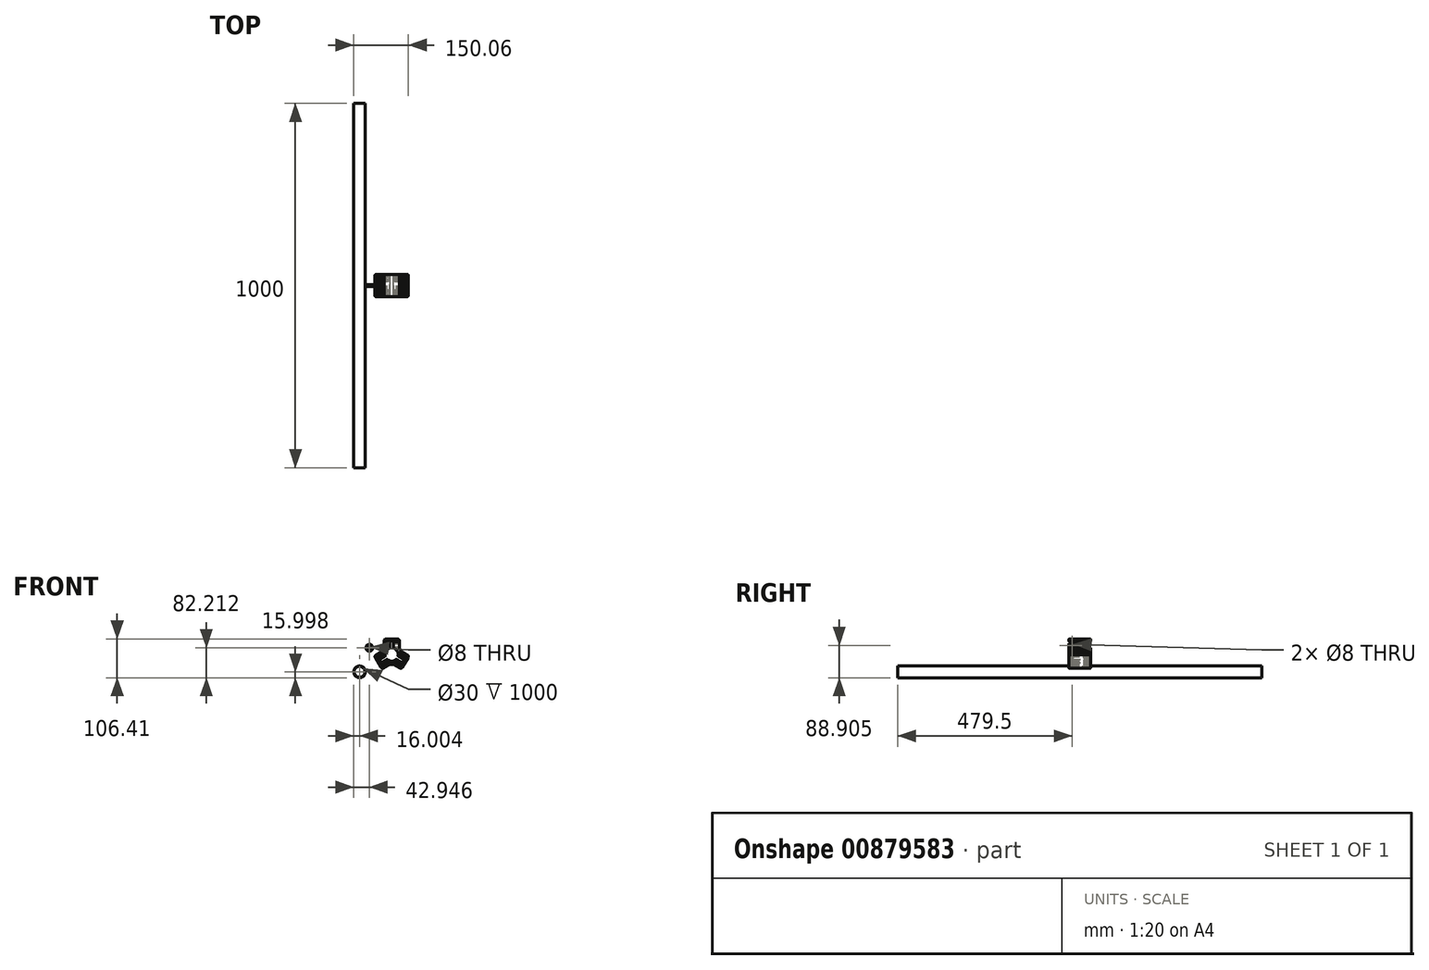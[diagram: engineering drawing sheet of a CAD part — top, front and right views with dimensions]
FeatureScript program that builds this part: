
annotation { "Feature Type Name" : "Feature", "Feature Type Description" : "" }
export const myFeature = defineFeature(function(context is Context, id is Id, definition is map)
    precondition{}
    {
        {
            var Q0;
            Q0=qCreatedBy(makeId("Front.planeOp"),FACE);
            var sketch = newSketch(context, id + "F0", { "sketchPlane" : qUnion([Q0])});
            skCircle(sketch, "E0", {"center": v(-38.83, 28.74) * mm, "radius": 9.5 * mm});
            skCircle(sketch, "E1", {"center": v(-38.83, 28.74) * mm, "radius": 4 * mm});
            skSolve(sketch);
        }
        {
            var Q0;
            Q0 = qSketchRegion(id + "F0", true);
            extrude(context, id + "F1", {"entities" : qUnion([Q0]), "endBound" : BoundingType.SYMMETRIC, "depth" : 6 * mm, "offsetDistance" : 25 * mm});
        }
        {
            var Q0;
            Q0=makeQuery(id+"F1.opExtrude","CAP_EDGE",EDGE,{"disambiguationData":[OSD([sQuery(id+"F0.wireOp",EDGE,"E0")])],"isStart":false});
            var Q1;
            Q1=makeQuery(id+"F1.opExtrude","CAP_EDGE",EDGE,{"disambiguationData":[OSD([sQuery(id+"F0.wireOp",EDGE,"E1")])],"isStart":false});
            var Q2;
            Q2=makeQuery(id+"F1.opExtrude","CAP_EDGE",EDGE,{"disambiguationData":[OSD([sQuery(id+"F0.wireOp",EDGE,"E0")])],"isStart":true});
            var Q3;
            Q3=makeQuery(id+"F1.opExtrude","CAP_EDGE",EDGE,{"disambiguationData":[OSD([sQuery(id+"F0.wireOp",EDGE,"E1")])],"isStart":true});
            fillet(context, id + "F2", {"entities" : qUnion([Q0, Q1, Q2, Q3]), "radius" : 0.2 * mm, "tangentPropagation" : true, "allowEdgeOverflow" : false});
        }
        {
            var Q0;
            Q0=qCreatedBy(makeId("Front.planeOp"),FACE);
            var sketch = newSketch(context, id + "F3", { "sketchPlane" : qUnion([Q0])});
            skCircle(sketch, "E2", {"center": v(22.48, 9.94) * mm, "radius": 16 * mm});
            skLineSegment(sketch, "E3.bottom", {"start": v(19.48, 25.94) * mm, "end": v(25.48, 25.94) * mm});
            skLineSegment(sketch, "E3.top", {"start": v(19.48, 44.94) * mm, "end": v(25.48, 44.94) * mm});
            skLineSegment(sketch, "E3.left", {"start": v(19.48, 25.94) * mm, "end": v(19.48, 44.94) * mm});
            skLineSegment(sketch, "E3.right", {"start": v(25.48, 25.94) * mm, "end": v(25.48, 44.94) * mm});
            skPoint(sketch, "E4", {"position": v(22.48, 25.94) * mm});
            skLineSegment(sketch, "E5.1.0", {"start": v(-6.33, -10.16) * mm, "end": v(-9.33, -4.97) * mm});
            skLineSegment(sketch, "E5.1.1", {"start": v(10.12, -0.66) * mm, "end": v(-6.33, -10.16) * mm});
            skLineSegment(sketch, "E5.1.2", {"start": v(7.12, 4.53) * mm, "end": v(-9.33, -4.97) * mm});
            skLineSegment(sketch, "E5.1.3", {"start": v(10.12, -0.66) * mm, "end": v(7.12, 4.53) * mm});
            skLineSegment(sketch, "E5.2.0", {"start": v(54.29, -4.97) * mm, "end": v(51.29, -10.16) * mm});
            skLineSegment(sketch, "E5.2.1", {"start": v(37.83, 4.53) * mm, "end": v(54.29, -4.97) * mm});
            skLineSegment(sketch, "E5.2.2", {"start": v(34.83, -0.66) * mm, "end": v(51.29, -10.16) * mm});
            skLineSegment(sketch, "E5.2.3", {"start": v(37.83, 4.53) * mm, "end": v(34.83, -0.66) * mm});
            skArc(sketch, "E6", {"start": v(16.18, 26.8) * mm, "mid": v(6.89, 18.93) * mm, "end": v(4.73, 6.96) * mm});
            skArc(sketch, "E7.trimOffspring", {"start": v(40.23, 6.96) * mm, "mid": v(38.06, 18.93) * mm, "end": v(28.78, 26.8) * mm});
            skArc(sketch, "E8.trimOffspring", {"start": v(11.03, -3.95) * mm, "mid": v(22.48, -8.06) * mm, "end": v(33.93, -3.95) * mm});
            skLineSegment(sketch, "E9.0", {"start": v(27.48, 28.67) * mm, "end": v(27.48, 45.94) * mm});
            skLineSegment(sketch, "E9.1", {"start": v(18.48, 46.94) * mm, "end": v(26.48, 46.94) * mm});
            skLineSegment(sketch, "E9.2", {"start": v(17.48, 28.67) * mm, "end": v(17.48, 45.94) * mm});
            skLineSegment(sketch, "E10", {"start": v(27.48, 46.94) * mm, "end": v(27.48, 52.94) * mm, "construction": true});
            skLineSegment(sketch, "E11", {"start": v(1.7, 27.32) * mm, "end": v(1.7, 47.94) * mm});
            skLineSegment(sketch, "E12", {"start": v(6.7, 52.94) * mm, "end": v(38.26, 52.94) * mm});
            skLineSegment(sketch, "E13.1.0", {"start": v(17.81, -16.76) * mm, "end": v(-0.04, -27.06) * mm});
            skLineSegment(sketch, "E13.1.1", {"start": v(-6.87, -25.23) * mm, "end": v(-22.65, 2.1) * mm});
            skLineSegment(sketch, "E13.1.2", {"start": v(-2.97, 19.24) * mm, "end": v(-20.82, 8.93) * mm});
            skLineSegment(sketch, "E13.2.0", {"start": v(47.92, 19.24) * mm, "end": v(65.78, 8.93) * mm});
            skLineSegment(sketch, "E13.2.1", {"start": v(67.6, 2.1) * mm, "end": v(51.82, -25.23) * mm});
            skLineSegment(sketch, "E13.2.2", {"start": v(27.14, -16.76) * mm, "end": v(45, -27.06) * mm});
            skPoint(sketch, "E14.visualSharp", {"position": v(1.7, 52.94) * mm});
            skArc(sketch, "E14.filletArc", {"start": v(6.7, 52.94) * mm, "mid": v(3.16, 51.47) * mm, "end": v(1.7, 47.94) * mm});
            skPoint(sketch, "E15.visualSharp", {"position": v(-25.15, 6.43) * mm});
            skArc(sketch, "E15.filletArc", {"start": v(-20.82, 8.93) * mm, "mid": v(-23.15, 5.9) * mm, "end": v(-22.65, 2.1) * mm});
            skPoint(sketch, "E16.visualSharp", {"position": v(-4.37, -29.56) * mm});
            skArc(sketch, "E16.filletArc", {"start": v(-6.87, -25.23) * mm, "mid": v(-3.84, -27.56) * mm, "end": v(-0.04, -27.06) * mm});
            skPoint(sketch, "E17.visualSharp", {"position": v(49.32, -29.56) * mm});
            skArc(sketch, "E17.filletArc", {"start": v(45, -27.06) * mm, "mid": v(48.79, -27.56) * mm, "end": v(51.82, -25.23) * mm});
            skPoint(sketch, "E18.visualSharp", {"position": v(70.1, 6.43) * mm});
            skArc(sketch, "E18.filletArc", {"start": v(67.6, 2.1) * mm, "mid": v(68.1, 5.9) * mm, "end": v(65.78, 8.93) * mm});
            skLineSegment(sketch, "E19", {"start": v(43.26, 47.94) * mm, "end": v(43.26, 27.32) * mm});
            skPoint(sketch, "E20.visualSharp", {"position": v(43.26, 52.94) * mm});
            skArc(sketch, "E20.filletArc", {"start": v(43.26, 47.94) * mm, "mid": v(41.8, 51.47) * mm, "end": v(38.26, 52.94) * mm});
            skLineSegment(sketch, "E21.1.0", {"start": v(8.75, -3.76) * mm, "end": v(-6.2, -12.4) * mm});
            skLineSegment(sketch, "E21.1.1", {"start": v(-7.57, -12.03) * mm, "end": v(-11.57, -5.1) * mm});
            skLineSegment(sketch, "E21.1.2", {"start": v(3.75, 4.9) * mm, "end": v(-11.2, -3.73) * mm});
            skLineSegment(sketch, "E21.2.0", {"start": v(41.2, 4.9) * mm, "end": v(56.15, -3.73) * mm});
            skLineSegment(sketch, "E21.2.1", {"start": v(56.52, -5.1) * mm, "end": v(52.52, -12.03) * mm});
            skLineSegment(sketch, "E21.2.2", {"start": v(36.2, -3.76) * mm, "end": v(51.15, -12.4) * mm});
            skPoint(sketch, "E22.visualSharp", {"position": v(10, -3.04) * mm});
            skArc(sketch, "E22.filletArc", {"start": v(11.03, -3.95) * mm, "mid": v(9.92, -3.5) * mm, "end": v(8.75, -3.76) * mm});
            skPoint(sketch, "E23.visualSharp", {"position": v(34.95, -3.04) * mm});
            skArc(sketch, "E23.filletArc", {"start": v(36.2, -3.76) * mm, "mid": v(35.03, -3.5) * mm, "end": v(33.93, -3.95) * mm});
            skPoint(sketch, "E24.visualSharp", {"position": v(39.95, 5.62) * mm});
            skArc(sketch, "E24.filletArc", {"start": v(40.23, 6.96) * mm, "mid": v(40.4, 5.78) * mm, "end": v(41.2, 4.9) * mm});
            skPoint(sketch, "E25.visualSharp", {"position": v(27.48, 27.22) * mm});
            skArc(sketch, "E25.filletArc", {"start": v(27.48, 28.67) * mm, "mid": v(27.83, 27.53) * mm, "end": v(28.78, 26.8) * mm});
            skPoint(sketch, "E26.visualSharp", {"position": v(17.48, 27.22) * mm});
            skArc(sketch, "E26.filletArc", {"start": v(16.18, 26.8) * mm, "mid": v(17.12, 27.53) * mm, "end": v(17.48, 28.67) * mm});
            skPoint(sketch, "E27.visualSharp", {"position": v(5, 5.62) * mm});
            skArc(sketch, "E27.filletArc", {"start": v(3.75, 4.9) * mm, "mid": v(4.56, 5.78) * mm, "end": v(4.73, 6.96) * mm});
            skPoint(sketch, "E28.visualSharp", {"position": v(17.48, 46.94) * mm});
            skArc(sketch, "E28.filletArc", {"start": v(18.48, 46.94) * mm, "mid": v(17.77, 46.64) * mm, "end": v(17.48, 45.94) * mm});
            skPoint(sketch, "E29.visualSharp", {"position": v(27.48, 46.94) * mm});
            skArc(sketch, "E29.filletArc", {"start": v(27.48, 45.94) * mm, "mid": v(27.18, 46.64) * mm, "end": v(26.48, 46.94) * mm});
            skPoint(sketch, "E30.visualSharp", {"position": v(57.02, -4.23) * mm});
            skArc(sketch, "E30.filletArc", {"start": v(56.52, -5.1) * mm, "mid": v(56.62, -4.34) * mm, "end": v(56.15, -3.73) * mm});
            skPoint(sketch, "E31.visualSharp", {"position": v(52.02, -12.9) * mm});
            skArc(sketch, "E31.filletArc", {"start": v(51.15, -12.4) * mm, "mid": v(51.91, -12.5) * mm, "end": v(52.52, -12.03) * mm});
            skPoint(sketch, "E32.visualSharp", {"position": v(-7.07, -12.9) * mm});
            skArc(sketch, "E32.filletArc", {"start": v(-7.57, -12.03) * mm, "mid": v(-6.96, -12.5) * mm, "end": v(-6.2, -12.4) * mm});
            skPoint(sketch, "E33.visualSharp", {"position": v(-12.07, -4.23) * mm});
            skArc(sketch, "E33.filletArc", {"start": v(-11.2, -3.73) * mm, "mid": v(-11.67, -4.34) * mm, "end": v(-11.57, -5.1) * mm});
            skArc(sketch, "E34", {"start": v(1.7, 27.32) * mm, "mid": v(-1, 23.48) * mm, "end": v(-2.97, 19.24) * mm});
            skArc(sketch, "E35.trimOffspring", {"start": v(47.92, 19.24) * mm, "mid": v(45.94, 23.48) * mm, "end": v(43.26, 27.32) * mm});
            skArc(sketch, "E36.trimOffspring", {"start": v(17.81, -16.76) * mm, "mid": v(22.48, -17.16) * mm, "end": v(27.14, -16.76) * mm});
            skPoint(sketch, "E37.orphan", {"position": v(1.7, 21.93) * mm});
            skPoint(sketch, "E38.orphan", {"position": v(43.26, 21.93) * mm});
            skPoint(sketch, "E39.orphan", {"position": v(22.48, -14.06) * mm});
            skSolve(sketch);
        }
        {
            var Q0;
            Q0 = qSketchRegion(id + "F3", true);
            extrude(context, id + "F4", {"entities" : qUnion([Q0]), "endBound" : BoundingType.SYMMETRIC, "depth" : 60 * mm, "offsetDistance" : 25 * mm});
        }
        {
            var Q0;
            Q0=makeQuery(id+"F4.opExtrude","SWEPT_FACE",FACE,{"disambiguationData":[OSD([sQuery(id+"F3.wireOp",EDGE,"E9.0")])]});
            var sketch = newSketch(context, id + "F5", { "sketchPlane" : qUnion([Q0])});
            skCircle(sketch, "E40", {"center": v(20.5, 35.44) * mm, "radius": 9.5 * mm});
            skPoint(sketch, "E41", {"position": v(30, 35.44) * mm});
            skPoint(sketch, "E42", {"position": v(20.5, 44.94) * mm});
            skCircle(sketch, "E43", {"center": v(20.5, 35.44) * mm, "radius": 4 * mm});
            skLineSegment(sketch, "E44", {"start": v(0, 28.67) * mm, "end": v(0, 37.9) * mm});
            skCircle(sketch, "E45.MirrorC", {"center": v(-20.5, 35.44) * mm, "radius": 4 * mm});
            skLineSegment(sketch, "E46", {"start": v(20.5, 35.44) * mm, "end": v(20.5, 28.67) * mm});
            skSolve(sketch);
        }
        {
            var Q0;
            Q0=makeQuery(id+"F5.imprint","IMPRINT",FACE,{"disambiguationData":[TD([[makeQuery(id+"F5.imprint","IMPRINT",EDGE,{"derivedFrom":sQuery(id+"F5.wireOp",EDGE,"E43")}),1.0]])]});
            extrude(context, id + "F6", {"entities" : qUnion([Q0]), "operationType" : NewBodyOperationType.REMOVE, "endBound" : BoundingType.SYMMETRIC, "depth" : 55.2 * mm, "offsetDistance" : 25 * mm});
        }
        {
            var Q0;
            Q0=makeQuery(id+"F5.imprint","IMPRINT",FACE,{"disambiguationData":[TD([[makeQuery(id+"F5.imprint","IMPRINT",EDGE,{"derivedFrom":sQuery(id+"F5.wireOp",EDGE,"E45.MirrorC")}),-1.0]])]});
            extrude(context, id + "F7", {"entities" : qUnion([Q0]), "operationType" : NewBodyOperationType.REMOVE, "endBound" : BoundingType.SYMMETRIC, "depth" : 66 * mm, "offsetDistance" : 25 * mm});
        }
        {
            var Q0;
            Q0=makeQuery(id+"F4.opExtrude","SWEPT_FACE",FACE,{"disambiguationData":[OSD([sQuery(id+"F3.wireOp",EDGE,"E21.1.0")])]});
            var sketch = newSketch(context, id + "F8", { "sketchPlane" : qUnion([Q0])});
            skCircle(sketch, "E47", {"center": v(-1.07, 20.5) * mm, "radius": 9.5 * mm});
            skPoint(sketch, "E48", {"position": v(-1.07, 30) * mm});
            skPoint(sketch, "E49", {"position": v(-10.57, 20.5) * mm});
            skCircle(sketch, "E50", {"center": v(-1.07, 20.5) * mm, "radius": 4 * mm});
            skLineSegment(sketch, "E51", {"start": v(5.7, 0) * mm, "end": v(-4.1, 0) * mm});
            skCircle(sketch, "E52.MirrorC", {"center": v(-1.07, -20.5) * mm, "radius": 4 * mm});
            skLineSegment(sketch, "E53", {"start": v(-1.07, 20.5) * mm, "end": v(5.7, 20.5) * mm});
            skSolve(sketch);
        }
        {
            var Q0;
            Q0=makeQuery(id+"F8.imprint","IMPRINT",FACE,{"disambiguationData":[TD([[makeQuery(id+"F8.imprint","IMPRINT",EDGE,{"derivedFrom":sQuery(id+"F8.wireOp",EDGE,"E52.MirrorC")}),-1.0]])]});
            var Q1;
            Q1=makeQuery(id+"F8.imprint","IMPRINT",FACE,{"disambiguationData":[TD([[makeQuery(id+"F8.imprint","IMPRINT",EDGE,{"derivedFrom":sQuery(id+"F8.wireOp",EDGE,"E50")}),1.0]])]});
            extrude(context, id + "F9", {"entities" : qUnion([Q0, Q1]), "operationType" : NewBodyOperationType.REMOVE, "endBound" : BoundingType.SYMMETRIC, "depth" : 59.8 * mm, "offsetDistance" : 25 * mm});
        }
        {
            var Q0;
            Q0=makeQuery(id+"F4.opExtrude","SWEPT_FACE",FACE,{"disambiguationData":[OSD([sQuery(id+"F3.wireOp",EDGE,"E21.2.0")])]});
            var sketch = newSketch(context, id + "F10", { "sketchPlane" : qUnion([Q0])});
            skCircle(sketch, "E54", {"center": v(40, -20.5) * mm, "radius": 9.5 * mm});
            skPoint(sketch, "E55", {"position": v(49.5, -20.5) * mm});
            skPoint(sketch, "E56", {"position": v(40, -30) * mm});
            skCircle(sketch, "E57", {"center": v(40, -20.5) * mm, "radius": 4 * mm});
            skLineSegment(sketch, "E58", {"start": v(33.23, 0) * mm, "end": v(40.2, 0) * mm});
            skCircle(sketch, "E59.MirrorC", {"center": v(40, 20.5) * mm, "radius": 4 * mm});
            skLineSegment(sketch, "E60", {"start": v(49.5, -20.5) * mm, "end": v(33.23, -20.5) * mm});
            skSolve(sketch);
        }
        {
            var Q0;
            Q0=makeQuery(id+"F10.imprint","IMPRINT",FACE,{"disambiguationData":[TD([[makeQuery(id+"F10.imprint","IMPRINT",EDGE,{"derivedFrom":sQuery(id+"F10.wireOp",EDGE,"E59.MirrorC")}),-1.0]])]});
            var Q1;
            Q1=makeQuery(id+"F10.imprint","IMPRINT",FACE,{"disambiguationData":[TD([[makeQuery(id+"F10.imprint","IMPRINT",EDGE,{"derivedFrom":sQuery(id+"F10.wireOp",EDGE,"E57")}),1.0]])]});
            extrude(context, id + "F11", {"entities" : qUnion([Q0, Q1]), "operationType" : NewBodyOperationType.REMOVE, "endBound" : BoundingType.SYMMETRIC, "depth" : 65.4 * mm, "offsetDistance" : 25 * mm});
        }
        {
            var Q0;
            Q0=makeQuery(id+"F4.opExtrude","CAP_FACE",FACE,{"disambiguationData":[OSD([sQuery(id+"F3.wireOp",EDGE,"E6"),sQuery(id+"F3.wireOp",EDGE,"E7.trimOffspring"),sQuery(id+"F3.wireOp",EDGE,"E8.trimOffspring"),sQuery(id+"F3.wireOp",EDGE,"E9.0"),sQuery(id+"F3.wireOp",EDGE,"E9.1"),sQuery(id+"F3.wireOp",EDGE,"E9.2"),sQuery(id+"F3.wireOp",EDGE,"E11"),sQuery(id+"F3.wireOp",EDGE,"E12"),sQuery(id+"F3.wireOp",EDGE,"E13.1.0"),sQuery(id+"F3.wireOp",EDGE,"E13.1.1"),sQuery(id+"F3.wireOp",EDGE,"E13.1.2"),sQuery(id+"F3.wireOp",EDGE,"E13.2.0"),sQuery(id+"F3.wireOp",EDGE,"E13.2.1"),sQuery(id+"F3.wireOp",EDGE,"E13.2.2"),sQuery(id+"F3.wireOp",EDGE,"E14.filletArc"),sQuery(id+"F3.wireOp",EDGE,"E15.filletArc"),sQuery(id+"F3.wireOp",EDGE,"E16.filletArc"),sQuery(id+"F3.wireOp",EDGE,"E17.filletArc"),sQuery(id+"F3.wireOp",EDGE,"E18.filletArc"),sQuery(id+"F3.wireOp",EDGE,"E19"),sQuery(id+"F3.wireOp",EDGE,"E20.filletArc"),sQuery(id+"F3.wireOp",EDGE,"E21.1.0"),sQuery(id+"F3.wireOp",EDGE,"E21.1.1"),sQuery(id+"F3.wireOp",EDGE,"E21.1.2"),sQuery(id+"F3.wireOp",EDGE,"E21.2.0"),sQuery(id+"F3.wireOp",EDGE,"E21.2.1"),sQuery(id+"F3.wireOp",EDGE,"E21.2.2"),sQuery(id+"F3.wireOp",EDGE,"E22.filletArc"),sQuery(id+"F3.wireOp",EDGE,"E23.filletArc"),sQuery(id+"F3.wireOp",EDGE,"E24.filletArc"),sQuery(id+"F3.wireOp",EDGE,"E25.filletArc"),sQuery(id+"F3.wireOp",EDGE,"E26.filletArc"),sQuery(id+"F3.wireOp",EDGE,"E27.filletArc"),sQuery(id+"F3.wireOp",EDGE,"E28.filletArc"),sQuery(id+"F3.wireOp",EDGE,"E29.filletArc"),sQuery(id+"F3.wireOp",EDGE,"E30.filletArc"),sQuery(id+"F3.wireOp",EDGE,"E31.filletArc"),sQuery(id+"F3.wireOp",EDGE,"E32.filletArc"),sQuery(id+"F3.wireOp",EDGE,"E33.filletArc")])],"isStart":true});
            var Q1;
            Q1=makeQuery(id+"F4.opExtrude","CAP_FACE",FACE,{"disambiguationData":[OSD([sQuery(id+"F3.wireOp",EDGE,"E6"),sQuery(id+"F3.wireOp",EDGE,"E7.trimOffspring"),sQuery(id+"F3.wireOp",EDGE,"E8.trimOffspring"),sQuery(id+"F3.wireOp",EDGE,"E9.0"),sQuery(id+"F3.wireOp",EDGE,"E9.1"),sQuery(id+"F3.wireOp",EDGE,"E9.2"),sQuery(id+"F3.wireOp",EDGE,"E11"),sQuery(id+"F3.wireOp",EDGE,"E12"),sQuery(id+"F3.wireOp",EDGE,"E13.1.0"),sQuery(id+"F3.wireOp",EDGE,"E13.1.1"),sQuery(id+"F3.wireOp",EDGE,"E13.1.2"),sQuery(id+"F3.wireOp",EDGE,"E13.2.0"),sQuery(id+"F3.wireOp",EDGE,"E13.2.1"),sQuery(id+"F3.wireOp",EDGE,"E13.2.2"),sQuery(id+"F3.wireOp",EDGE,"E14.filletArc"),sQuery(id+"F3.wireOp",EDGE,"E15.filletArc"),sQuery(id+"F3.wireOp",EDGE,"E16.filletArc"),sQuery(id+"F3.wireOp",EDGE,"E17.filletArc"),sQuery(id+"F3.wireOp",EDGE,"E18.filletArc"),sQuery(id+"F3.wireOp",EDGE,"E19"),sQuery(id+"F3.wireOp",EDGE,"E20.filletArc"),sQuery(id+"F3.wireOp",EDGE,"E21.1.0"),sQuery(id+"F3.wireOp",EDGE,"E21.1.1"),sQuery(id+"F3.wireOp",EDGE,"E21.1.2"),sQuery(id+"F3.wireOp",EDGE,"E21.2.0"),sQuery(id+"F3.wireOp",EDGE,"E21.2.1"),sQuery(id+"F3.wireOp",EDGE,"E21.2.2"),sQuery(id+"F3.wireOp",EDGE,"E22.filletArc"),sQuery(id+"F3.wireOp",EDGE,"E23.filletArc"),sQuery(id+"F3.wireOp",EDGE,"E24.filletArc"),sQuery(id+"F3.wireOp",EDGE,"E25.filletArc"),sQuery(id+"F3.wireOp",EDGE,"E26.filletArc"),sQuery(id+"F3.wireOp",EDGE,"E27.filletArc"),sQuery(id+"F3.wireOp",EDGE,"E28.filletArc"),sQuery(id+"F3.wireOp",EDGE,"E29.filletArc"),sQuery(id+"F3.wireOp",EDGE,"E30.filletArc"),sQuery(id+"F3.wireOp",EDGE,"E31.filletArc"),sQuery(id+"F3.wireOp",EDGE,"E32.filletArc"),sQuery(id+"F3.wireOp",EDGE,"E33.filletArc")])],"isStart":false});
            fillet(context, id + "F12", {"entities" : qUnion([Q0, Q1]), "radius" : 2 * mm, "tangentPropagation" : true, "allowEdgeOverflow" : false});
        }
        {
            var Q0;
            Q0=qCreatedBy(makeId("Front.planeOp"),FACE);
            var sketch = newSketch(context, id + "F13", { "sketchPlane" : qUnion([Q0])});
            skCircle(sketch, "E61", {"center": v(-65.78, -37.47) * mm, "radius": 16 * mm});
            skCircle(sketch, "E62", {"center": v(-65.78, -37.47) * mm, "radius": 15 * mm});
            skSolve(sketch);
        }
        {
            var Q0;
            Q0 = qSketchRegion(id + "F13", true);
            extrude(context, id + "F14", {"entities" : qUnion([Q0]), "endBound" : BoundingType.SYMMETRIC, "depth" : 1000 * mm, "offsetDistance" : 25 * mm});
        }
    });
